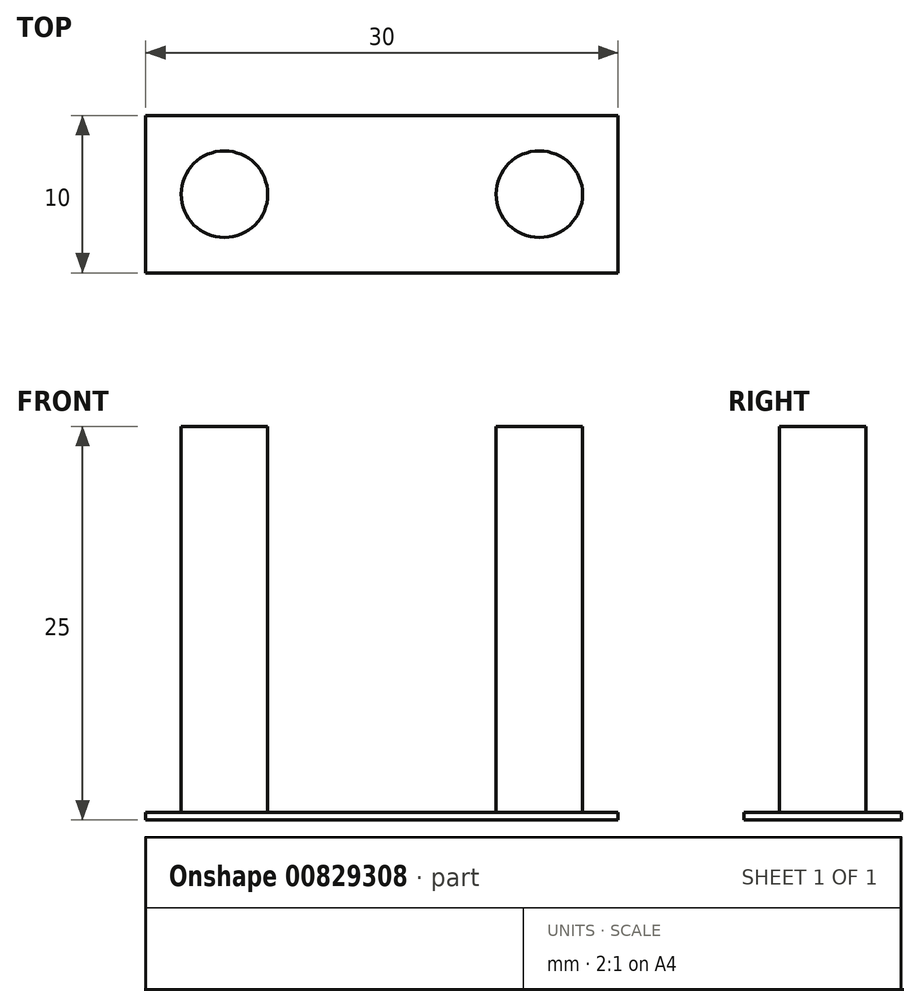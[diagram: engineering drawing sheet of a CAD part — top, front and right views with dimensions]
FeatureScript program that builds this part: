
annotation { "Feature Type Name" : "Feature", "Feature Type Description" : "" }
export const myFeature = defineFeature(function(context is Context, id is Id, definition is map)
    precondition{}
    {
        {
            var Q0;
            Q0=qCreatedBy(makeId("Top.planeOp"),FACE);
            var sketch = newSketch(context, id + "F0", { "sketchPlane" : qUnion([Q0])});
            skLineSegment(sketch, "E0.bottom", {"start": v(15, 5) * mm, "end": v(-15, 5) * mm});
            skLineSegment(sketch, "E0.top", {"start": v(15, -5) * mm, "end": v(-15, -5) * mm});
            skLineSegment(sketch, "E0.left", {"start": v(15, 5) * mm, "end": v(15, -5) * mm});
            skLineSegment(sketch, "E0.right", {"start": v(-15, 5) * mm, "end": v(-15, -5) * mm});
            skPoint(sketch, "E0.middle", {"position": v(0, 0) * mm});
            skLineSegment(sketch, "E1", {"start": v(-15, 0) * mm, "end": v(-10, 0) * mm});
            skLineSegment(sketch, "E2", {"start": v(-10, 0) * mm, "end": v(10, 0) * mm});
            skLineSegment(sketch, "E3", {"start": v(10, 0) * mm, "end": v(15, 0) * mm});
            skCircle(sketch, "E4", {"center": v(-10, 0) * mm, "radius": 2.75 * mm});
            skCircle(sketch, "E5", {"center": v(10, 0) * mm, "radius": 2.75 * mm});
            skSolve(sketch);
        }
        {
            var Q0;
            Q0 = qSketchRegion(id + "F0", true);
            extrude(context, id + "F1", {"entities" : qUnion([Q0]), "depth" : .5 * mm, "offsetDistance" : 25 * mm});
        }
        {
            var Q0;
            {var subQ0=sQuery(id+"F0.wireOp",EDGE,"E2");var subQ1=sQuery(id+"F0.wireOp",EDGE,"E1");var subQ2=makeQuery(id+"F0.imprint","INTERSECT",VERTEX,{"derivedFrom":[subQ1,subQ0]});Q0=makeQuery(id+"F0.imprint","IMPRINT",FACE,{"disambiguationData":[TD([[makeQuery(id+"F0.imprint","IMPRINT",EDGE,{"disambiguationData":[TD([[subQ2,1.0]])],"derivedFrom":subQ1}),1.0]])]});}
            var Q1;
            {var subQ0=sQuery(id+"F0.wireOp",EDGE,"E2");var subQ1=sQuery(id+"F0.wireOp",EDGE,"E1");var subQ2=makeQuery(id+"F0.imprint","INTERSECT",VERTEX,{"derivedFrom":[subQ1,subQ0]});Q1=makeQuery(id+"F0.imprint","IMPRINT",FACE,{"disambiguationData":[TD([[makeQuery(id+"F0.imprint","IMPRINT",EDGE,{"disambiguationData":[TD([[subQ2,1.0]])],"derivedFrom":subQ1}),-1.0]])]});}
            var Q2;
            {var subQ0=sQuery(id+"F0.wireOp",EDGE,"E3");var subQ1=sQuery(id+"F0.wireOp",EDGE,"E2");var subQ2=makeQuery(id+"F0.imprint","INTERSECT",VERTEX,{"derivedFrom":[subQ1,subQ0]});Q2=makeQuery(id+"F0.imprint","IMPRINT",FACE,{"disambiguationData":[TD([[makeQuery(id+"F0.imprint","IMPRINT",EDGE,{"disambiguationData":[TD([[subQ2,1.0]])],"derivedFrom":subQ1}),1.0]])]});}
            var Q3;
            {var subQ0=sQuery(id+"F0.wireOp",EDGE,"E3");var subQ1=sQuery(id+"F0.wireOp",EDGE,"E2");var subQ2=makeQuery(id+"F0.imprint","INTERSECT",VERTEX,{"derivedFrom":[subQ1,subQ0]});Q3=makeQuery(id+"F0.imprint","IMPRINT",FACE,{"disambiguationData":[TD([[makeQuery(id+"F0.imprint","IMPRINT",EDGE,{"disambiguationData":[TD([[subQ2,1.0]])],"derivedFrom":subQ1}),-1.0]])]});}
            extrude(context, id + "F2", {"entities" : qUnion([Q0, Q1, Q2, Q3]), "operationType" : NewBodyOperationType.ADD, "depth" : 25 * mm, "offsetDistance" : 25 * mm});
        }
    });
